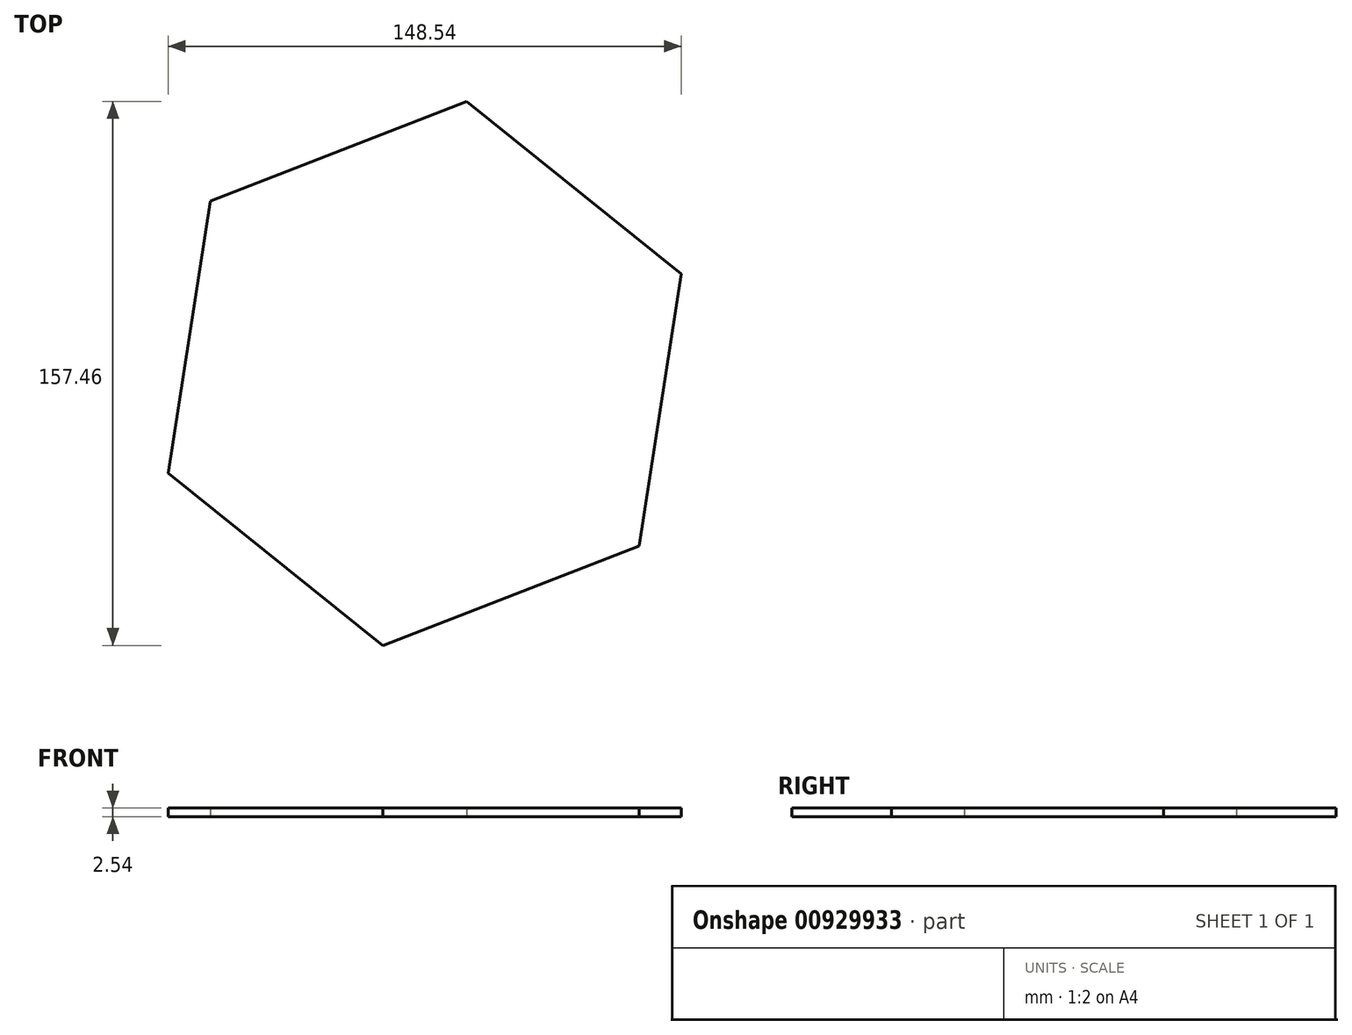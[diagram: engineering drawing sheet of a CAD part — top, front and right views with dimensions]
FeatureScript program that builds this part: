
annotation { "Feature Type Name" : "Feature", "Feature Type Description" : "" }
export const myFeature = defineFeature(function(context is Context, id is Id, definition is map)
    precondition{}
    {
        {
            var Q0;
            Q0=qCreatedBy(makeId("Top.planeOp"),FACE);
            var sketch = newSketch(context, id + "F0", { "sketchPlane" : qUnion([Q0])});
            skCircle(sketch, "E0.cCircle", {"center": v(0, 0) * mm, "radius": 69 * mm, "construction": true});
            skLineSegment(sketch, "E0.0", {"start": v(12.19, 78.73) * mm, "end": v(74.27, 28.8) * mm});
            skLineSegment(sketch, "E0.1", {"start": v(74.27, 28.8) * mm, "end": v(62.09, -49.92) * mm});
            skLineSegment(sketch, "E0.2", {"start": v(62.09, -49.92) * mm, "end": v(-12.19, -78.73) * mm});
            skLineSegment(sketch, "E0.3", {"start": v(-12.19, -78.73) * mm, "end": v(-74.27, -28.8) * mm});
            skLineSegment(sketch, "E0.4", {"start": v(-74.27, -28.8) * mm, "end": v(-62.09, 49.92) * mm});
            skLineSegment(sketch, "E0.5", {"start": v(-62.09, 49.92) * mm, "end": v(12.19, 78.73) * mm});
            skPoint(sketch, "E0.0.midPoint", {"position": v(43.23, 53.77) * mm});
            skSolve(sketch);
        }
        {
            var Q0;
            Q0=makeQuery(id+"F0.imprint","IMPRINT",FACE,{"disambiguationData":[TD([[makeQuery(id+"F0.imprint","IMPRINT",EDGE,{"derivedFrom":sQuery(id+"F0.wireOp",EDGE,"E0.0")}),-1.0]])]});
            extrude(context, id + "F1", {"entities" : qUnion([Q0]), "depth" : 2.54 * mm, "offsetDistance" : 25.4 * mm});
        }
    });
